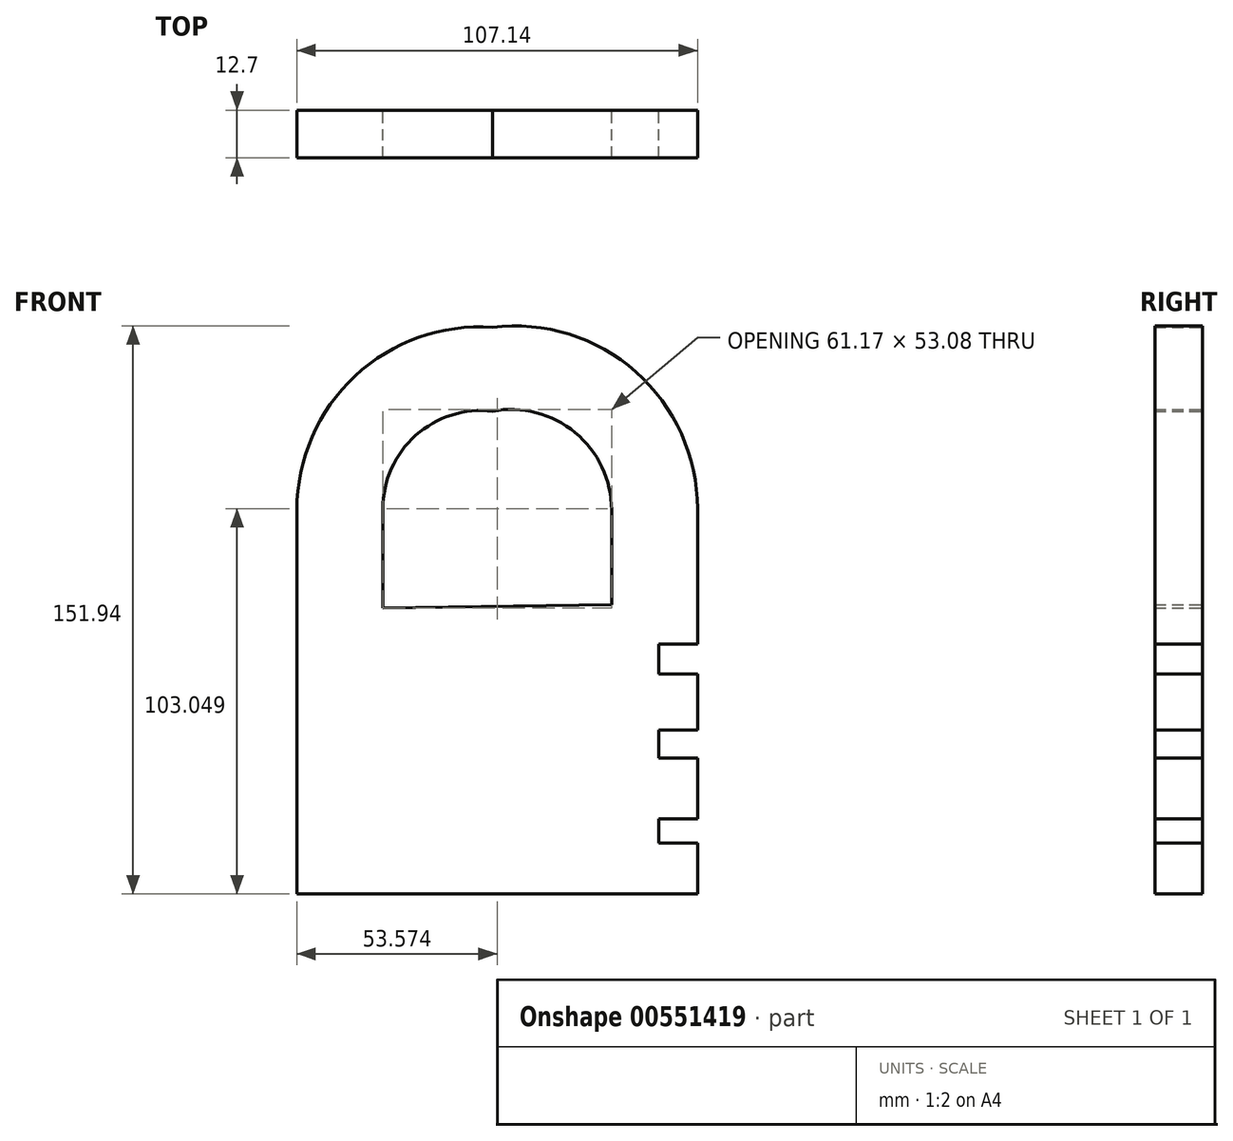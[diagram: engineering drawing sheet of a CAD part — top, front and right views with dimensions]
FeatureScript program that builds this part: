
annotation { "Feature Type Name" : "Feature", "Feature Type Description" : "" }
export const myFeature = defineFeature(function(context is Context, id is Id, definition is map)
    precondition{}
    {
        {
            var Q0;
            Q0=qCreatedBy(makeId("Front.planeOp"),FACE);
            var sketch = newSketch(context, id + "F0", { "sketchPlane" : qUnion([Q0])});
            skLineSegment(sketch, "E0", {"start": v(-52.32, 53.67) * mm, "end": v(-52.32, -22.53) * mm});
            skLineSegment(sketch, "E1", {"start": v(-52.32, -22.53) * mm, "end": v(54.82, -22.53) * mm});
            skLineSegment(sketch, "E2", {"start": v(54.82, 55.11) * mm, "end": v(-52.32, 53.67) * mm});
            skLineSegment(sketch, "E3", {"start": v(-52.32, 53.67) * mm, "end": v(-52.32, 65.9) * mm});
            skLineSegment(sketch, "E4", {"start": v(-52.32, 65.9) * mm, "end": v(-52.32, 80.2) * mm});
            skLineSegment(sketch, "E5", {"start": v(-52.32, 80.2) * mm, "end": v(-29.33, 80.51) * mm});
            skLineSegment(sketch, "E6", {"start": v(-29.33, 80.51) * mm, "end": v(-29.33, 53.67) * mm});
            skLineSegment(sketch, "E7", {"start": v(-29.33, 53.67) * mm, "end": v(-52.32, 53.67) * mm});
            skLineSegment(sketch, "E8", {"start": v(54.82, 55.11) * mm, "end": v(54.82, 80.51) * mm});
            skLineSegment(sketch, "E9", {"start": v(54.82, 80.51) * mm, "end": v(31.84, 80.2) * mm});
            skLineSegment(sketch, "E10", {"start": v(31.84, 80.2) * mm, "end": v(31.84, 54.8) * mm});
            skLineSegment(sketch, "E11", {"start": v(31.84, 54.8) * mm, "end": v(54.82, 55.11) * mm});
            skArc(sketch, "E12", {"start": v(0, 129.05) * mm, "mid": v(-36.77, 116) * mm, "end": v(-52.32, 80.2) * mm});
            skArc(sketch, "E13", {"start": v(0, 106.61) * mm, "mid": v(-20.52, 100.14) * mm, "end": v(-29.33, 80.51) * mm});
            skLineSegment(sketch, "E14", {"start": v(0, 129.05) * mm, "end": v(0, 106.61) * mm});
            skArc(sketch, "E15", {"start": v(31.84, 80.2) * mm, "mid": v(22.12, 100.89) * mm, "end": v(0, 106.61) * mm});
            skArc(sketch, "E16", {"start": v(54.82, 80.51) * mm, "mid": v(38.34, 117.13) * mm, "end": v(0, 129.05) * mm});
            skLineSegment(sketch, "E17.bottom", {"start": v(54.82, 21.31) * mm, "end": v(44.48, 21.31) * mm});
            skLineSegment(sketch, "E17.top", {"start": v(54.82, 13.83) * mm, "end": v(44.48, 13.83) * mm});
            skLineSegment(sketch, "E17.right", {"start": v(44.48, 21.31) * mm, "end": v(44.48, 13.83) * mm});
            skLineSegment(sketch, "E18.bottom", {"start": v(54.82, 44.36) * mm, "end": v(44.48, 44.36) * mm});
            skLineSegment(sketch, "E18.top", {"start": v(54.82, 36.26) * mm, "end": v(44.48, 36.26) * mm});
            skLineSegment(sketch, "E18.right", {"start": v(44.48, 44.36) * mm, "end": v(44.48, 36.26) * mm});
            skLineSegment(sketch, "E19.bottom", {"start": v(54.82, -2.37) * mm, "end": v(44.48, -2.37) * mm});
            skLineSegment(sketch, "E19.top", {"start": v(54.82, -8.9) * mm, "end": v(44.48, -8.9) * mm});
            skLineSegment(sketch, "E19.right", {"start": v(44.48, -2.37) * mm, "end": v(44.48, -8.9) * mm});
            skLineSegment(sketch, "E20", {"start": v(54.82, 55.11) * mm, "end": v(54.82, 44.36) * mm});
            skLineSegment(sketch, "E21", {"start": v(54.82, 36.26) * mm, "end": v(54.82, 21.31) * mm});
            skLineSegment(sketch, "E22", {"start": v(54.82, -2.37) * mm, "end": v(54.82, 13.83) * mm});
            skLineSegment(sketch, "E23", {"start": v(54.82, -22.53) * mm, "end": v(54.82, -8.9) * mm});
            skSolve(sketch);
        }
        {
            var Q0;
            Q0=makeQuery(id+"F0.imprint","IMPRINT",FACE,{"disambiguationData":[TD([[makeQuery(id+"F0.imprint","IMPRINT",EDGE,{"derivedFrom":sQuery(id+"F0.wireOp",EDGE,"E0")}),1.0]])]});
            extrude(context, id + "F1", {"entities" : qUnion([Q0]), "depth" : 6.35 * mm, "offsetDistance" : 25.4 * mm});
        }
        {
            var Q0;
            Q0 = qSketchRegion(id + "F0", true);
            extrude(context, id + "F2", {"entities" : qUnion([Q0]), "operationType" : NewBodyOperationType.ADD, "depth" : 12.7 * mm, "offsetDistance" : 25.4 * mm});
        }
    });
